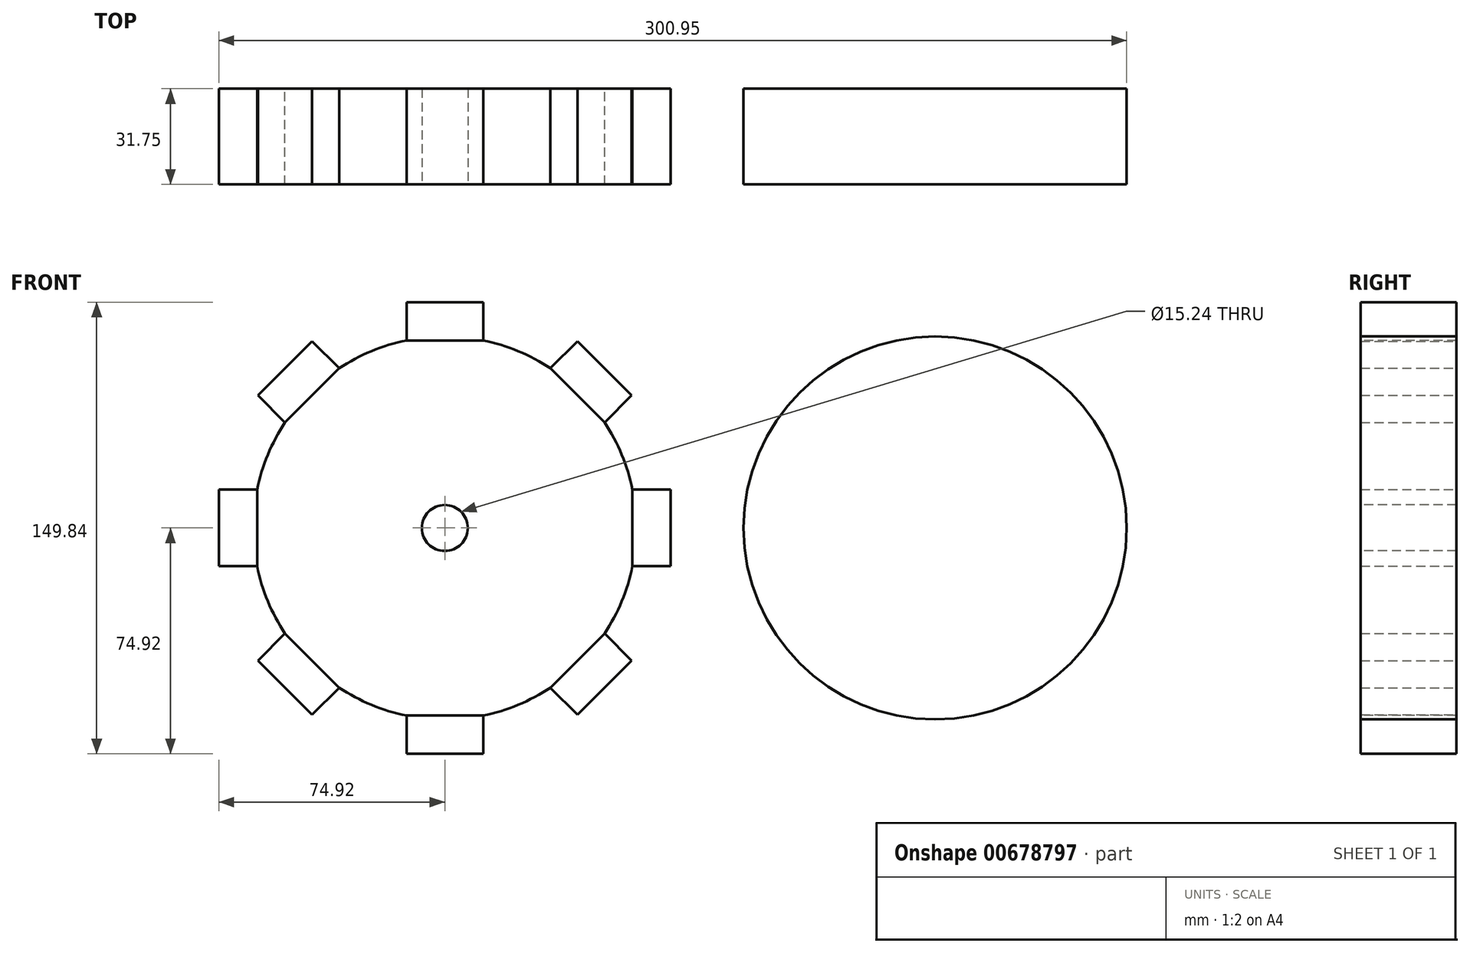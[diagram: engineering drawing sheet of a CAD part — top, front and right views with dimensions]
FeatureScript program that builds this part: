
annotation { "Feature Type Name" : "Feature", "Feature Type Description" : "" }
export const myFeature = defineFeature(function(context is Context, id is Id, definition is map)
    precondition{}
    {
        {
            var Q0;
            Q0=qCreatedBy(makeId("Front.planeOp"),FACE);
            var sketch = newSketch(context, id + "F0", { "sketchPlane" : qUnion([Q0])});
            skCircle(sketch, "E0", {"center": v(0, 0) * mm, "radius": 63.5 * mm});
            skSolve(sketch);
        }
        {
            var Q0;
            Q0 = qSketchRegion(id + "F0", true);
            extrude(context, id + "F1", {"entities" : qUnion([Q0]), "depth" : 31.75 * mm, "offsetDistance" : 25.4 * mm});
        }
        {
            var Q0;
            Q0=makeQuery(id+"FXcHTLzZ7Fd5Oc8_1.boolean.opBoolean","MERGE",FACE,{"derivedFrom":[makeQuery(id+"F1.opExtrude","CAP_FACE",FACE,{"disambiguationData":[OSD([sQuery(id+"F0.wireOp",EDGE,"E0")])],"isStart":false}),makeQuery(id+"FXcHTLzZ7Fd5Oc8_1.opExtrude","CAP_FACE",FACE,{"disambiguationData":[OSD([sQuery(id+"FTH1MoRm93BAgTd_1.wireOp",EDGE,"pJ2rFkAh-9EX0-jNcB-WvNr-GvZ3n7dj2FTq.bottom"),sQuery(id+"FTH1MoRm93BAgTd_1.wireOp",EDGE,"pJ2rFkAh-9EX0-jNcB-WvNr-GvZ3n7dj2FTq.top"),sQuery(id+"FTH1MoRm93BAgTd_1.wireOp",EDGE,"pJ2rFkAh-9EX0-jNcB-WvNr-GvZ3n7dj2FTq.left"),sQuery(id+"FTH1MoRm93BAgTd_1.wireOp",EDGE,"pJ2rFkAh-9EX0-jNcB-WvNr-GvZ3n7dj2FTq.right")])],"isStart":false}),makeQuery(id+"FXcHTLzZ7Fd5Oc8_1.opExtrude","CAP_FACE",FACE,{"disambiguationData":[OSD([sQuery(id+"FTH1MoRm93BAgTd_1.wireOp",EDGE,"45ef5a58-c318-428c-b637-5cee166f87a5.1.0"),sQuery(id+"FTH1MoRm93BAgTd_1.wireOp",EDGE,"45ef5a58-c318-428c-b637-5cee166f87a5.1.1"),sQuery(id+"FTH1MoRm93BAgTd_1.wireOp",EDGE,"45ef5a58-c318-428c-b637-5cee166f87a5.1.2"),sQuery(id+"FTH1MoRm93BAgTd_1.wireOp",EDGE,"45ef5a58-c318-428c-b637-5cee166f87a5.1.3")])],"isStart":false}),makeQuery(id+"FXcHTLzZ7Fd5Oc8_1.opExtrude","CAP_FACE",FACE,{"disambiguationData":[OSD([sQuery(id+"FTH1MoRm93BAgTd_1.wireOp",EDGE,"45ef5a58-c318-428c-b637-5cee166f87a5.2.0"),sQuery(id+"FTH1MoRm93BAgTd_1.wireOp",EDGE,"45ef5a58-c318-428c-b637-5cee166f87a5.2.1"),sQuery(id+"FTH1MoRm93BAgTd_1.wireOp",EDGE,"45ef5a58-c318-428c-b637-5cee166f87a5.2.2"),sQuery(id+"FTH1MoRm93BAgTd_1.wireOp",EDGE,"45ef5a58-c318-428c-b637-5cee166f87a5.2.3")])],"isStart":false}),makeQuery(id+"FXcHTLzZ7Fd5Oc8_1.opExtrude","CAP_FACE",FACE,{"disambiguationData":[OSD([sQuery(id+"FTH1MoRm93BAgTd_1.wireOp",EDGE,"45ef5a58-c318-428c-b637-5cee166f87a5.3.0"),sQuery(id+"FTH1MoRm93BAgTd_1.wireOp",EDGE,"45ef5a58-c318-428c-b637-5cee166f87a5.3.1"),sQuery(id+"FTH1MoRm93BAgTd_1.wireOp",EDGE,"45ef5a58-c318-428c-b637-5cee166f87a5.3.2"),sQuery(id+"FTH1MoRm93BAgTd_1.wireOp",EDGE,"45ef5a58-c318-428c-b637-5cee166f87a5.3.3")])],"isStart":false}),makeQuery(id+"FXcHTLzZ7Fd5Oc8_1.opExtrude","CAP_FACE",FACE,{"disambiguationData":[OSD([sQuery(id+"FTH1MoRm93BAgTd_1.wireOp",EDGE,"45ef5a58-c318-428c-b637-5cee166f87a5.4.0"),sQuery(id+"FTH1MoRm93BAgTd_1.wireOp",EDGE,"45ef5a58-c318-428c-b637-5cee166f87a5.4.1"),sQuery(id+"FTH1MoRm93BAgTd_1.wireOp",EDGE,"45ef5a58-c318-428c-b637-5cee166f87a5.4.2"),sQuery(id+"FTH1MoRm93BAgTd_1.wireOp",EDGE,"45ef5a58-c318-428c-b637-5cee166f87a5.4.3")])],"isStart":false}),makeQuery(id+"FXcHTLzZ7Fd5Oc8_1.opExtrude","CAP_FACE",FACE,{"disambiguationData":[OSD([sQuery(id+"FTH1MoRm93BAgTd_1.wireOp",EDGE,"45ef5a58-c318-428c-b637-5cee166f87a5.5.0"),sQuery(id+"FTH1MoRm93BAgTd_1.wireOp",EDGE,"45ef5a58-c318-428c-b637-5cee166f87a5.5.1"),sQuery(id+"FTH1MoRm93BAgTd_1.wireOp",EDGE,"45ef5a58-c318-428c-b637-5cee166f87a5.5.2"),sQuery(id+"FTH1MoRm93BAgTd_1.wireOp",EDGE,"45ef5a58-c318-428c-b637-5cee166f87a5.5.3")])],"isStart":false}),makeQuery(id+"FXcHTLzZ7Fd5Oc8_1.opExtrude","CAP_FACE",FACE,{"disambiguationData":[OSD([sQuery(id+"FTH1MoRm93BAgTd_1.wireOp",EDGE,"45ef5a58-c318-428c-b637-5cee166f87a5.6.0"),sQuery(id+"FTH1MoRm93BAgTd_1.wireOp",EDGE,"45ef5a58-c318-428c-b637-5cee166f87a5.6.1"),sQuery(id+"FTH1MoRm93BAgTd_1.wireOp",EDGE,"45ef5a58-c318-428c-b637-5cee166f87a5.6.2"),sQuery(id+"FTH1MoRm93BAgTd_1.wireOp",EDGE,"45ef5a58-c318-428c-b637-5cee166f87a5.6.3")])],"isStart":false}),makeQuery(id+"FXcHTLzZ7Fd5Oc8_1.opExtrude","CAP_FACE",FACE,{"disambiguationData":[OSD([sQuery(id+"FTH1MoRm93BAgTd_1.wireOp",EDGE,"45ef5a58-c318-428c-b637-5cee166f87a5.7.0"),sQuery(id+"FTH1MoRm93BAgTd_1.wireOp",EDGE,"45ef5a58-c318-428c-b637-5cee166f87a5.7.1"),sQuery(id+"FTH1MoRm93BAgTd_1.wireOp",EDGE,"45ef5a58-c318-428c-b637-5cee166f87a5.7.2"),sQuery(id+"FTH1MoRm93BAgTd_1.wireOp",EDGE,"45ef5a58-c318-428c-b637-5cee166f87a5.7.3")])],"isStart":false})]});
            var sketch = newSketch(context, id + "F2", { "sketchPlane" : qUnion([Q0])});
            skLineSegment(sketch, "E1", {"start": v(-12.7, 62.22) * mm, "end": v(12.7, 62.22) * mm});
            skPoint(sketch, "E2.center", {"position": v(0, 0) * mm});
            skArc(sketch, "E3", {"start": v(12.7, 62.22) * mm, "mid": v(0, 63.5) * mm, "end": v(-12.7, 62.22) * mm});
            skArc(sketch, "E4.1.0", {"start": v(-35.01, 52.97) * mm, "mid": v(-44.9, 44.9) * mm, "end": v(-52.97, 35.01) * mm});
            skLineSegment(sketch, "E4.1.1", {"start": v(-52.97, 35.01) * mm, "end": v(-35.01, 52.97) * mm});
            skArc(sketch, "E4.2.0", {"start": v(-62.22, 12.7) * mm, "mid": v(-63.5, 0) * mm, "end": v(-62.22, -12.7) * mm});
            skLineSegment(sketch, "E4.2.1", {"start": v(-62.22, -12.7) * mm, "end": v(-62.22, 12.7) * mm});
            skArc(sketch, "E4.3.0", {"start": v(-52.97, -35.01) * mm, "mid": v(-44.9, -44.9) * mm, "end": v(-35.01, -52.97) * mm});
            skLineSegment(sketch, "E4.3.1", {"start": v(-35.01, -52.97) * mm, "end": v(-52.97, -35.01) * mm});
            skArc(sketch, "E4.4.0", {"start": v(-12.7, -62.22) * mm, "mid": v(0, -63.5) * mm, "end": v(12.7, -62.22) * mm});
            skLineSegment(sketch, "E4.4.1", {"start": v(12.7, -62.22) * mm, "end": v(-12.7, -62.22) * mm});
            skArc(sketch, "E4.5.0", {"start": v(35.01, -52.97) * mm, "mid": v(44.9, -44.9) * mm, "end": v(52.97, -35.01) * mm});
            skLineSegment(sketch, "E4.5.1", {"start": v(52.97, -35.01) * mm, "end": v(35.01, -52.97) * mm});
            skArc(sketch, "E4.6.0", {"start": v(62.22, -12.7) * mm, "mid": v(63.5, 0) * mm, "end": v(62.22, 12.7) * mm});
            skLineSegment(sketch, "E4.6.1", {"start": v(62.22, 12.7) * mm, "end": v(62.22, -12.7) * mm});
            skArc(sketch, "E4.7.0", {"start": v(52.97, 35.01) * mm, "mid": v(44.9, 44.9) * mm, "end": v(35.01, 52.97) * mm});
            skLineSegment(sketch, "E4.7.1", {"start": v(35.01, 52.97) * mm, "end": v(52.97, 35.01) * mm});
            skSolve(sketch);
        }
        {
            var Q0;
            Q0 = qSketchRegion(id + "F2", true);
            extrude(context, id + "F3", {"entities" : qUnion([Q0]), "operationType" : NewBodyOperationType.REMOVE, "oppositeDirection" : true, "depth" : 31.75 * mm, "offsetDistance" : 25.4 * mm});
        }
        {
            var Q0;
            Q0=qCreatedBy(makeId("Front.planeOp"),FACE);
            var sketch = newSketch(context, id + "F4", { "sketchPlane" : qUnion([Q0])});
            skLineSegment(sketch, "E5.bottom", {"start": v(-12.7, 62.22) * mm, "end": v(12.7, 62.22) * mm});
            skLineSegment(sketch, "E5.top", {"start": v(-12.7, 74.92) * mm, "end": v(12.7, 74.92) * mm});
            skLineSegment(sketch, "E5.left", {"start": v(-12.7, 62.22) * mm, "end": v(-12.7, 74.92) * mm});
            skLineSegment(sketch, "E5.right", {"start": v(12.7, 62.22) * mm, "end": v(12.7, 74.92) * mm});
            skLineSegment(sketch, "E6.1.0", {"start": v(-61.95, 44) * mm, "end": v(-44, 61.95) * mm});
            skLineSegment(sketch, "E6.1.1", {"start": v(-52.97, 35.01) * mm, "end": v(-61.95, 44) * mm});
            skLineSegment(sketch, "E6.1.2", {"start": v(-52.97, 35.01) * mm, "end": v(-35.01, 52.97) * mm});
            skLineSegment(sketch, "E6.1.3", {"start": v(-35.01, 52.97) * mm, "end": v(-44, 61.95) * mm});
            skLineSegment(sketch, "E6.2.0", {"start": v(-74.92, -12.7) * mm, "end": v(-74.92, 12.7) * mm});
            skLineSegment(sketch, "E6.2.1", {"start": v(-62.22, -12.7) * mm, "end": v(-74.92, -12.7) * mm});
            skLineSegment(sketch, "E6.2.2", {"start": v(-62.22, -12.7) * mm, "end": v(-62.22, 12.7) * mm});
            skLineSegment(sketch, "E6.2.3", {"start": v(-62.22, 12.7) * mm, "end": v(-74.92, 12.7) * mm});
            skLineSegment(sketch, "E6.3.0", {"start": v(-44, -61.95) * mm, "end": v(-61.95, -44) * mm});
            skLineSegment(sketch, "E6.3.1", {"start": v(-35.01, -52.97) * mm, "end": v(-44, -61.95) * mm});
            skLineSegment(sketch, "E6.3.2", {"start": v(-35.01, -52.97) * mm, "end": v(-52.97, -35.01) * mm});
            skLineSegment(sketch, "E6.3.3", {"start": v(-52.97, -35.01) * mm, "end": v(-61.95, -44) * mm});
            skLineSegment(sketch, "E6.4.0", {"start": v(12.7, -74.92) * mm, "end": v(-12.7, -74.92) * mm});
            skLineSegment(sketch, "E6.4.1", {"start": v(12.7, -62.22) * mm, "end": v(12.7, -74.92) * mm});
            skLineSegment(sketch, "E6.4.2", {"start": v(12.7, -62.22) * mm, "end": v(-12.7, -62.22) * mm});
            skLineSegment(sketch, "E6.4.3", {"start": v(-12.7, -62.22) * mm, "end": v(-12.7, -74.92) * mm});
            skLineSegment(sketch, "E6.5.0", {"start": v(61.95, -44) * mm, "end": v(44, -61.95) * mm});
            skLineSegment(sketch, "E6.5.1", {"start": v(52.97, -35.01) * mm, "end": v(61.95, -44) * mm});
            skLineSegment(sketch, "E6.5.2", {"start": v(52.97, -35.01) * mm, "end": v(35.01, -52.97) * mm});
            skLineSegment(sketch, "E6.5.3", {"start": v(35.01, -52.97) * mm, "end": v(44, -61.95) * mm});
            skLineSegment(sketch, "E6.6.0", {"start": v(74.92, 12.7) * mm, "end": v(74.92, -12.7) * mm});
            skLineSegment(sketch, "E6.6.1", {"start": v(62.22, 12.7) * mm, "end": v(74.92, 12.7) * mm});
            skLineSegment(sketch, "E6.6.2", {"start": v(62.22, 12.7) * mm, "end": v(62.22, -12.7) * mm});
            skLineSegment(sketch, "E6.6.3", {"start": v(62.22, -12.7) * mm, "end": v(74.92, -12.7) * mm});
            skLineSegment(sketch, "E6.7.0", {"start": v(44, 61.95) * mm, "end": v(61.95, 44) * mm});
            skLineSegment(sketch, "E6.7.1", {"start": v(35.01, 52.97) * mm, "end": v(44, 61.95) * mm});
            skLineSegment(sketch, "E6.7.2", {"start": v(35.01, 52.97) * mm, "end": v(52.97, 35.01) * mm});
            skLineSegment(sketch, "E6.7.3", {"start": v(52.97, 35.01) * mm, "end": v(61.95, 44) * mm});
            skPoint(sketch, "E6.center", {"position": v(0, 0) * mm});
            skSolve(sketch);
        }
        {
            var Q0;
            Q0 = qSketchRegion(id + "F4", true);
            extrude(context, id + "F5", {"entities" : qUnion([Q0]), "depth" : 31.75 * mm, "offsetDistance" : 25.4 * mm});
        }
        {
            var Q0;
            Q0=makeQuery(id+"F1.opExtrude","CAP_FACE",FACE,{"disambiguationData":[OSD([sQuery(id+"F0.wireOp",EDGE,"E0")])],"isStart":false});
            var sketch = newSketch(context, id + "F6", { "sketchPlane" : qUnion([Q0])});
            skCircle(sketch, "E7", {"center": v(0, 0) * mm, "radius": 7.62 * mm});
            skSolve(sketch);
        }
        {
            var Q0;
            Q0 = qSketchRegion(id + "F6", true);
            extrude(context, id + "F7", {"entities" : qUnion([Q0]), "operationType" : NewBodyOperationType.REMOVE, "oppositeDirection" : true, "depth" : 31.75 * mm, "offsetDistance" : 25.4 * mm});
        }
        {
            var Q0;
            Q0=qCreatedBy(makeId("Front.planeOp"),FACE);
            var sketch = newSketch(context, id + "F8", { "sketchPlane" : qUnion([Q0])});
            skArc(sketch, "E8", {"start": v(100.32, 12.7) * mm, "mid": v(99.03, 0) * mm, "end": v(100.32, -12.7) * mm});
            skCircle(sketch, "E9", {"center": v(162.53, 0) * mm, "radius": 63.5 * mm});
            skSolve(sketch);
        }
        {
            var Q0;
            Q0 = qSketchRegion(id + "F8", true);
            extrude(context, id + "F9", {"entities" : qUnion([Q0]), "depth" : 31.75 * mm, "offsetDistance" : 25.4 * mm});
        }
    });
